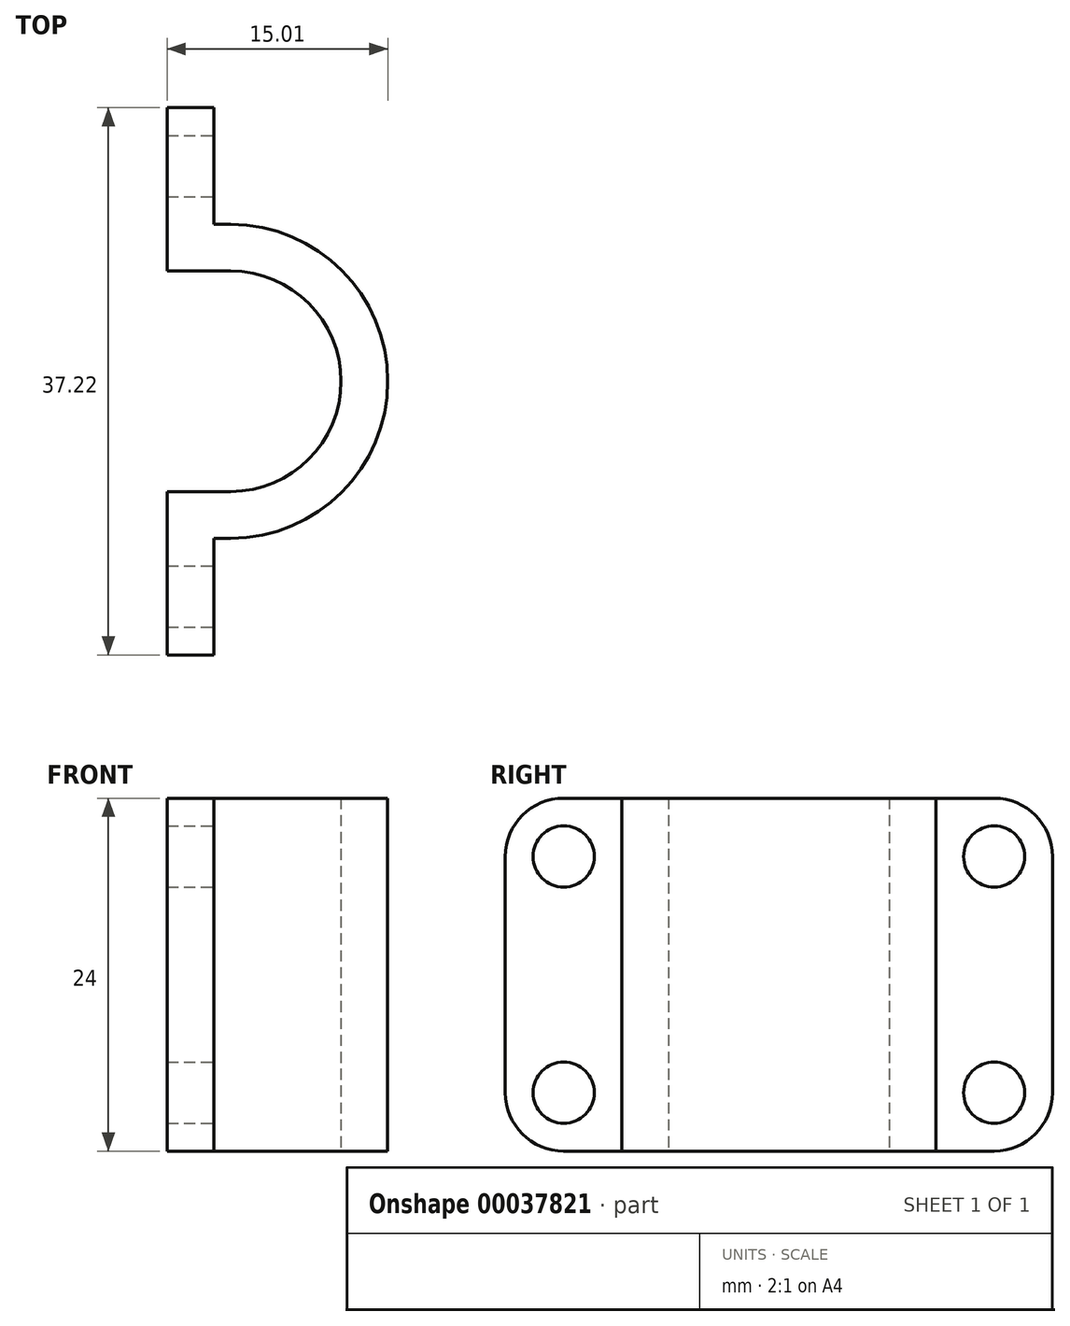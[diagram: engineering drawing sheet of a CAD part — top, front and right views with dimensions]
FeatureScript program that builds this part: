
annotation { "Feature Type Name" : "Feature", "Feature Type Description" : "" }
export const myFeature = defineFeature(function(context is Context, id is Id, definition is map)
    precondition{}
    {
        {
            var Q0;
            Q0=qCreatedBy(makeId("Top.planeOp"),FACE);
            var sketch = newSketch(context, id + "F0", { "sketchPlane" : qUnion([Q0])});
            skLineSegment(sketch, "E0", {"start": v(0, -7.5) * mm, "end": v(0, 7.5) * mm, "construction": true});
            skArc(sketch, "E1", {"start": v(0, -7.5) * mm, "mid": v(7.5, 0) * mm, "end": v(0, 7.5) * mm});
            skLineSegment(sketch, "E2", {"start": v(0, -7.5) * mm, "end": v(-4.32, -7.5) * mm});
            skLineSegment(sketch, "E3", {"start": v(0, 7.5) * mm, "end": v(-4.33, 7.5) * mm});
            skLineSegment(sketch, "E4", {"start": v(-4.33, 7.5) * mm, "end": v(-4.33, 18.61) * mm});
            skLineSegment(sketch, "E5", {"start": v(-4.33, 18.61) * mm, "end": v(-1.15, 18.61) * mm});
            skLineSegment(sketch, "E6", {"start": v(-1.15, 18.61) * mm, "end": v(-1.15, 10.67) * mm});
            skLineSegment(sketch, "E7", {"start": v(-1.15, 10.67) * mm, "end": v(0, 10.67) * mm});
            skLineSegment(sketch, "E8", {"start": v(0, 7.5) * mm, "end": v(0, 10.67) * mm, "construction": true});
            skLineSegment(sketch, "E9", {"start": v(0, -7.5) * mm, "end": v(0, -10.67) * mm, "construction": true});
            skLineSegment(sketch, "E10", {"start": v(0, -10.67) * mm, "end": v(-1.15, -10.67) * mm});
            skLineSegment(sketch, "E11", {"start": v(-1.15, -10.67) * mm, "end": v(-1.15, -18.61) * mm});
            skLineSegment(sketch, "E12", {"start": v(-1.15, -18.61) * mm, "end": v(-4.32, -18.61) * mm});
            skLineSegment(sketch, "E13", {"start": v(-4.32, -18.61) * mm, "end": v(-4.32, -7.5) * mm});
            skCircle(sketch, "E14", {"center": v(0, 0) * mm, "radius": 7.5 * mm, "construction": true});
            skLineSegment(sketch, "E15", {"start": v(0, 0) * mm, "end": v(-4.32, 0) * mm, "construction": true});
            skLineSegment(sketch, "E16", {"start": v(-4.32, 0) * mm, "end": v(-7.5, 0) * mm, "construction": true});
            skLineSegment(sketch, "E17", {"start": v(-4.33, 7.5) * mm, "end": v(-4.33, -7.5) * mm, "construction": true});
            skArc(sketch, "E18", {"start": v(0, -10.67) * mm, "mid": v(10.67, 0) * mm, "end": v(0, 10.67) * mm});
            skSolve(sketch);
        }
        {
            var Q0;
            Q0=qSketchRegion(id+"F0",true);
            extrude(context, id + "F1", {"entities" : qUnion([Q0]), "depth" : 24 * mm});
        }
        {
            var Q0;
            Q0=makeQuery(id+"F1.opExtrude","CAP_EDGE",EDGE,{"disambiguationData":[OSD([sQuery(id+"F0.wireOp",EDGE,"E12")])],"isStart":true});
            var Q1;
            Q1=makeQuery(id+"F1.opExtrude","CAP_EDGE",EDGE,{"disambiguationData":[OSD([sQuery(id+"F0.wireOp",EDGE,"E5")])],"isStart":true});
            var Q2;
            Q2=makeQuery(id+"F1.opExtrude","CAP_EDGE",EDGE,{"disambiguationData":[OSD([sQuery(id+"F0.wireOp",EDGE,"E5")])],"isStart":false});
            var Q3;
            Q3=makeQuery(id+"F1.opExtrude","CAP_EDGE",EDGE,{"disambiguationData":[OSD([sQuery(id+"F0.wireOp",EDGE,"E12")])],"isStart":false});
            fillet(context, id + "F2", {"entities" : qUnion([Q0, Q1, Q2, Q3]), "radius" : 3.97 * mm, "tangentPropagation" : true, "allowEdgeOverflow" : false});
        }
        {
            var Q0;
            Q0=makeQuery(id+"F1.opExtrude","SWEPT_FACE",FACE,{"disambiguationData":[OSD([sQuery(id+"F0.wireOp",EDGE,"E11")])]});
            var sketch = newSketch(context, id + "F3", { "sketchPlane" : qUnion([Q0])});
            skCircle(sketch, "E19", {"center": v(-14.64, 20.03) * mm, "radius": 2.08 * mm});
            skCircle(sketch, "E20", {"center": v(-14.64, 3.97) * mm, "radius": 2.08 * mm});
            skCircle(sketch, "E21", {"center": v(14.64, 3.97) * mm, "radius": 2.08 * mm});
            skCircle(sketch, "E22", {"center": v(14.64, 20.03) * mm, "radius": 2.08 * mm});
            skSolve(sketch);
        }
        {
            var Q0;
            Q0=qSketchRegion(id+"F3",true);
            var Q1;
            Q1=makeQuery(id+"F1.opExtrude","SWEPT_FACE",FACE,{"disambiguationData":[OSD([sQuery(id+"F0.wireOp",EDGE,"E13")])]});
            extrude(context, id + "F4", {"entities" : qUnion([Q0]), "operationType" : NewBodyOperationType.REMOVE, "endBound" : BoundingType.UP_TO_SURFACE, "oppositeDirection" : true, "endBoundEntityFace" : qUnion([Q1]), "depth" : 25.4 * mm});
        }
    });
